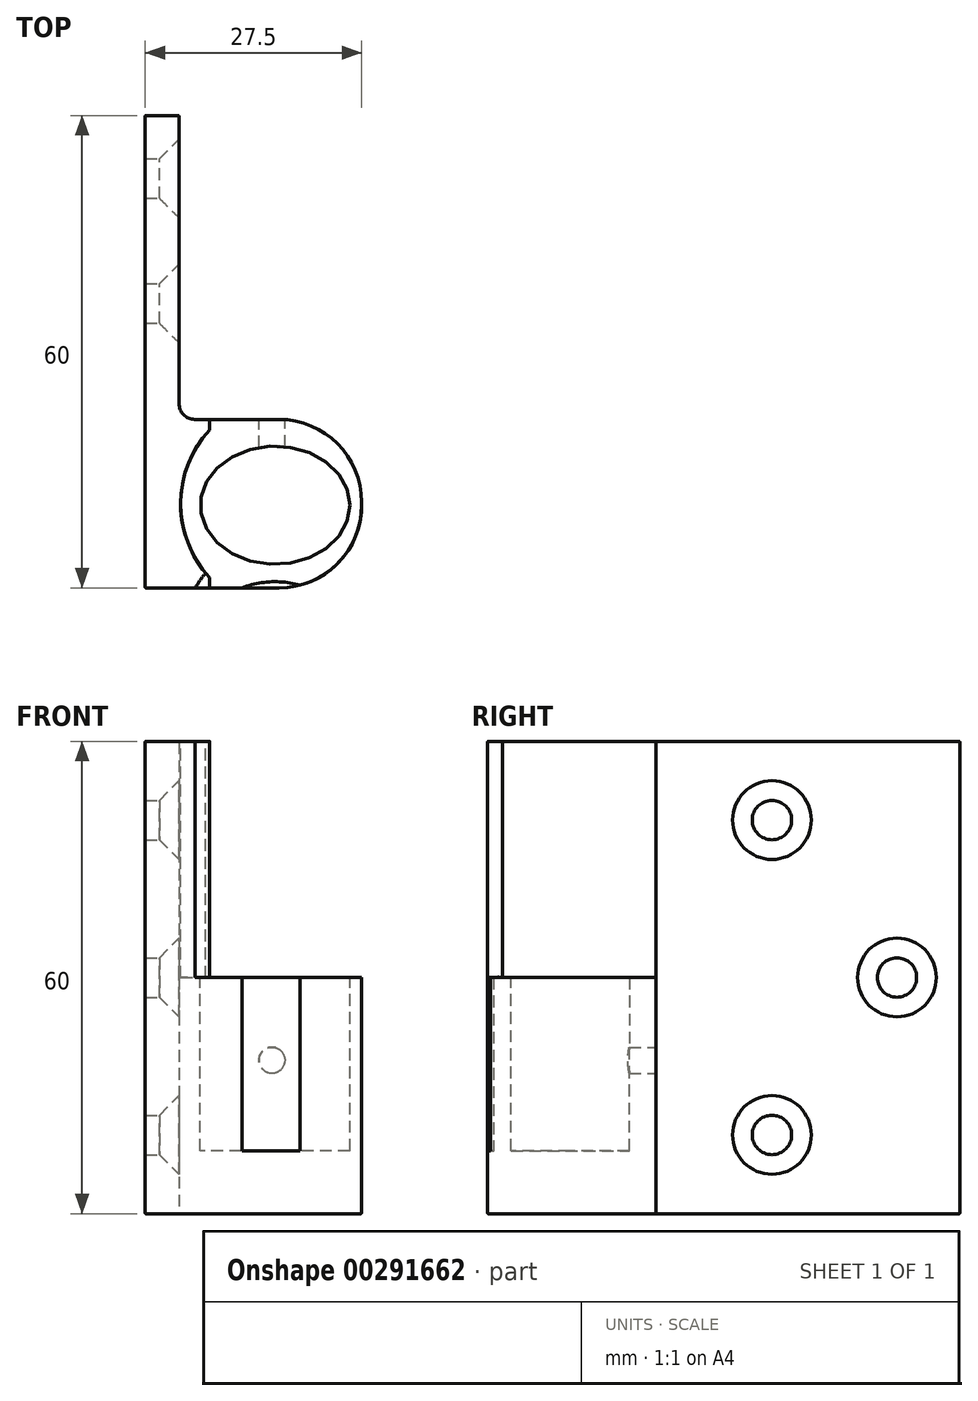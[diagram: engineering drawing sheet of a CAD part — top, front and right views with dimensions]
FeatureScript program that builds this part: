
annotation { "Feature Type Name" : "Feature", "Feature Type Description" : "" }
export const myFeature = defineFeature(function(context is Context, id is Id, definition is map)
    precondition{}
    {
        {
            var Q0;
            Q0=qCreatedBy(makeId("Top.planeOp"),FACE);
            var sketch = newSketch(context, id + "F0", { "sketchPlane" : qUnion([Q0])});
            skLineSegment(sketch, "E0", {"start": v(23.73, 6) * mm, "end": v(23.73, 6.4) * mm});
            skArc(sketch, "E1.filletArc", {"start": v(13.23, -4.5) * mm, "mid": v(20.66, -1.43) * mm, "end": v(23.73, 6) * mm});
            skArc(sketch, "E2.filletArc", {"start": v(23.73, 6.4) * mm, "mid": v(20.66, 13.82) * mm, "end": v(13.23, 16.9) * mm});
            skLineSegment(sketch, "E3.bottom", {"start": v(-3.77, -43.1) * mm, "end": v(0.53, -43.1) * mm});
            skLineSegment(sketch, "E3.left", {"start": v(-3.77, -43.1) * mm, "end": v(-3.77, 16.9) * mm});
            skLineSegment(sketch, "E3.right", {"start": v(0.53, -43.1) * mm, "end": v(0.53, -6.5) * mm});
            skLineSegment(sketch, "E4", {"start": v(-3.77, 16.9) * mm, "end": v(13.23, 16.9) * mm});
            skLineSegment(sketch, "E5", {"start": v(13.23, -4.5) * mm, "end": v(2.53, -4.5) * mm});
            skPoint(sketch, "E6.visualSharp", {"position": v(0.53, -4.5) * mm});
            skArc(sketch, "E6.filletArc", {"start": v(2.53, -4.5) * mm, "mid": v(1.12, -5.1) * mm, "end": v(0.53, -6.5) * mm});
            skSolve(sketch);
        }
        {
            var Q0;
            Q0=qSketchRegion(id+"F0",true);
            extrude(context, id + "F1", {"entities" : qUnion([Q0]), "depth" : 60 * mm});
        }
        {
            var Q0;
            Q0=makeQuery(id+"F1.opExtrude","CAP_FACE",FACE,{"disambiguationData":[OSD([sQuery(id+"F0.wireOp",EDGE,"E0"),sQuery(id+"F0.wireOp",EDGE,"E1.filletArc"),sQuery(id+"F0.wireOp",EDGE,"E2.filletArc"),sQuery(id+"F0.wireOp",EDGE,"E3.bottom"),sQuery(id+"F0.wireOp",EDGE,"E3.left"),sQuery(id+"F0.wireOp",EDGE,"E3.right"),sQuery(id+"F0.wireOp",EDGE,"E4"),sQuery(id+"F0.wireOp",EDGE,"E5"),sQuery(id+"F0.wireOp",EDGE,"E6.filletArc")])],"isStart":false});
            var sketch = newSketch(context, id + "F2", { "sketchPlane" : qUnion([Q0])});
            skLineSegment(sketch, "E7", {"start": v(4.43, 16.9) * mm, "end": v(4.43, 15.6) * mm});
            skLineSegment(sketch, "E8", {"start": v(-3.77, -4.5) * mm, "end": v(4.43, -4.5) * mm});
            skArc(sketch, "E9", {"start": v(4.43, 15.6) * mm, "mid": v(0.73, 6.2) * mm, "end": v(4.43, -3.2) * mm});
            skLineSegment(sketch, "E10", {"start": v(4.43, 16.9) * mm, "end": v(-3.77, 16.9) * mm});
            skLineSegment(sketch, "E11", {"start": v(-3.77, 16.9) * mm, "end": v(-3.77, -4.5) * mm});
            skLineSegment(sketch, "E12.trimOffspring", {"start": v(4.43, -3.2) * mm, "end": v(4.43, -4.5) * mm});
            skSolve(sketch);
        }
        {
            var Q0;
            {var subQ3=sQuery(id+"F2.wireOp",EDGE,"E7");Q0=makeQuery(id+"F2.imprint","IMPRINT",FACE,{"disambiguationData":[TD([[makeQuery(id+"F2.imprint","IMPRINT",EDGE,{"derivedFrom":subQ3}),1.0]])]});}
            extrude(context, id + "F3", {"entities" : qUnion([Q0]), "operationType" : NewBodyOperationType.REMOVE, "oppositeDirection" : true, "depth" : 30 * mm});
        }
        {
            var Q0;
            Q0=makeQuery(id+"F3.boolean.opBoolean","COPY",FACE,{"derivedFrom":makeQuery(id+"F3.opExtrude","CAP_FACE",FACE,{"disambiguationData":[OSD([sQuery(id+"F0.wireOp",EDGE,"E0"),sQuery(id+"F0.wireOp",EDGE,"E1.filletArc"),sQuery(id+"F0.wireOp",EDGE,"E2.filletArc"),sQuery(id+"F0.wireOp",EDGE,"E4"),sQuery(id+"F0.wireOp",EDGE,"E5"),sQuery(id+"F2.wireOp",EDGE,"E7"),sQuery(id+"F2.wireOp",EDGE,"E9"),sQuery(id+"F2.wireOp",EDGE,"E12.trimOffspring")])],"isStart":false})});
            var sketch = newSketch(context, id + "F4", { "sketchPlane" : qUnion([Q0])});
            skEllipse(sketch, "E13", {"center": v(12.73, 6.4) * mm, "majorRadius": 9.5 * mm, "minorRadius": 7.5 * mm, "majorAxis": v(1, 0)});
            skSolve(sketch);
        }
        {
            var Q0;
            Q0=makeQuery(id+"F4.imprint","IMPRINT",FACE,{"disambiguationData":[TD([[makeQuery(id+"F4.imprint","IMPRINT",EDGE,{"derivedFrom":sQuery(id+"F4.wireOp",EDGE,"E13")}),1.0]])]});
            extrude(context, id + "F5", {"entities" : qUnion([Q0]), "operationType" : NewBodyOperationType.REMOVE, "oppositeDirection" : true, "depth" : 22 * mm});
        }
        {
            var Q0;
            Q0=makeQuery(id+"F1.opExtrude","SWEPT_FACE",FACE,{"disambiguationData":[OSD([sQuery(id+"F0.wireOp",EDGE,"E5")])]});
            var sketch = newSketch(context, id + "F6", { "sketchPlane" : qUnion([Q0])});
            skCircle(sketch, "E14", {"center": v(12.33, 19.5) * mm, "radius": 1.5 * mm});
            skSolve(sketch);
        }
        {
            var Q0;
            Q0=sQuery(id+"F6.wireOp",VERTEX,"E14.center");
            var Q1;
            Q1=makeQuery(id+"F1.opExtrude","SWEPT_BODY",BODY,{"disambiguationData":[OSD([sQuery(id+"F0.wireOp",EDGE,"E0"),sQuery(id+"F0.wireOp",EDGE,"E1.filletArc"),sQuery(id+"F0.wireOp",EDGE,"E2.filletArc"),sQuery(id+"F0.wireOp",EDGE,"E3.bottom"),sQuery(id+"F0.wireOp",EDGE,"E3.left"),sQuery(id+"F0.wireOp",EDGE,"E3.right"),sQuery(id+"F0.wireOp",EDGE,"E4"),sQuery(id+"F0.wireOp",EDGE,"E5"),sQuery(id+"F0.wireOp",EDGE,"E6.filletArc")])]});
            hole(context, id + "F7", {"style" : HoleStyle.SIMPLE, "endStyle" : HoleEndStyle.BLIND, "standardTappedOrClearance" : lookupTablePath({ "standard" : "ISO", "fit" : "Normal", "size" : "M3", "type" : "Clearance" }), "standardBlindInLast" : lookupTablePath({ "fit" : "Standard", "standard" : "ISO", "size" : "M3", "type" : "Clearance" }), "holeDiameter" : 3.3 * mm, "holeDepth" : 8 * mm, "tappedDepth" : 10 * mm, "tapClearance" : 3, "locations" : qUnion([Q0]), "scope" : qUnion([Q1])});
        }
        {
            var Q0;
            Q0=makeQuery(id+"F1.opExtrude","SWEPT_FACE",FACE,{"disambiguationData":[OSD([sQuery(id+"F0.wireOp",EDGE,"E3.right")])]});
            var sketch = newSketch(context, id + "F8", { "sketchPlane" : qUnion([Q0])});
            skCircle(sketch, "E15", {"center": v(-19.23, 50) * mm, "radius": 2.5 * mm});
            skCircle(sketch, "E16", {"center": v(-35.1, 30) * mm, "radius": 2.5 * mm});
            skCircle(sketch, "E17", {"center": v(-19.23, 10) * mm, "radius": 2.5 * mm});
            skSolve(sketch);
        }
        {
            var Q0;
            Q0=sQuery(id+"F8.wireOp",VERTEX,"E15.center");
            var Q1;
            Q1=sQuery(id+"F8.wireOp",VERTEX,"E16.center");
            var Q2;
            Q2=sQuery(id+"F8.wireOp",VERTEX,"E17.center");
            var Q3;
            Q3=makeQuery(id+"F1.opExtrude","SWEPT_BODY",BODY,{"disambiguationData":[OSD([sQuery(id+"F0.wireOp",EDGE,"E0"),sQuery(id+"F0.wireOp",EDGE,"E1.filletArc"),sQuery(id+"F0.wireOp",EDGE,"E2.filletArc"),sQuery(id+"F0.wireOp",EDGE,"E3.bottom"),sQuery(id+"F0.wireOp",EDGE,"E3.left"),sQuery(id+"F0.wireOp",EDGE,"E3.right"),sQuery(id+"F0.wireOp",EDGE,"E4"),sQuery(id+"F0.wireOp",EDGE,"E5"),sQuery(id+"F0.wireOp",EDGE,"E6.filletArc")])]});
            hole(context, id + "F9", {"style" : HoleStyle.C_SINK, "endStyle" : HoleEndStyle.THROUGH, "holeDiameter" : 5 * mm, "cSinkDiameter" : 10 * mm, "cSinkAngle" : 90 * degree, "tappedDepth" : 10 * mm, "tapClearance" : 3, "locations" : qUnion([Q0, Q1, Q2]), "scope" : qUnion([Q3])});
        }
        {
            var Q0;
            Q0=makeQuery(id+"F1.opExtrude","CAP_EDGE",EDGE,{"disambiguationData":[OSD([sQuery(id+"F0.wireOp",EDGE,"E3.right")])],"isStart":false});
            var Q1;
            Q1=makeQuery(id+"F1.opExtrude","SWEPT_EDGE",EDGE,{"disambiguationData":[OSD([sQuery(id+"F0.wireOp",EDGE,"E3.bottom"),sQuery(id+"F0.wireOp",EDGE,"E3.right")])]});
            var Q2;
            Q2=makeQuery(id+"F1.opExtrude","CAP_EDGE",EDGE,{"disambiguationData":[OSD([sQuery(id+"F0.wireOp",EDGE,"E3.bottom")])],"isStart":false});
            var Q3;
            Q3=makeQuery(id+"F1.opExtrude","SWEPT_EDGE",EDGE,{"disambiguationData":[OSD([sQuery(id+"F0.wireOp",EDGE,"E3.bottom"),sQuery(id+"F0.wireOp",EDGE,"E3.left")])]});
            var Q4;
            Q4=makeQuery(id+"F1.opExtrude","CAP_EDGE",EDGE,{"disambiguationData":[OSD([sQuery(id+"F0.wireOp",EDGE,"E3.left")])],"isStart":false});
            var Q5;
            Q5=makeQuery(id+"F1.opExtrude","CAP_EDGE",EDGE,{"disambiguationData":[OSD([sQuery(id+"F0.wireOp",EDGE,"E3.bottom")])],"isStart":true});
            var Q6;
            Q6=makeQuery(id+"F1.opExtrude","CAP_EDGE",EDGE,{"disambiguationData":[OSD([sQuery(id+"F0.wireOp",EDGE,"E3.right")])],"isStart":true});
            var Q7;
            Q7=makeQuery(id+"F1.opExtrude","CAP_EDGE",EDGE,{"disambiguationData":[OSD([sQuery(id+"F0.wireOp",EDGE,"E3.left")])],"isStart":true});
            var Q8;
            Q8=makeQuery(id+"F1.opExtrude","SWEPT_EDGE",EDGE,{"disambiguationData":[OSD([sQuery(id+"F0.wireOp",EDGE,"E3.left"),sQuery(id+"F0.wireOp",EDGE,"E4")])]});
            var Q9;
            Q9=makeQuery(id+"F1.opExtrude","CAP_EDGE",EDGE,{"disambiguationData":[OSD([sQuery(id+"F0.wireOp",EDGE,"E4")])],"isStart":false});
            var Q10;
            Q10=makeQuery(id+"F3.boolean.opBoolean","COPY",EDGE,{"derivedFrom":makeQuery(id+"F3.opExtrude","CAP_EDGE",EDGE,{"disambiguationData":[OSD([sQuery(id+"F2.wireOp",EDGE,"E7")])],"isStart":true})});
            var Q11;
            Q11=makeQuery(id+"F1.opExtrude","CAP_EDGE",EDGE,{"disambiguationData":[OSD([sQuery(id+"F0.wireOp",EDGE,"E4")])],"isStart":true});
            var Q12;
            Q12=makeQuery(id+"F3.boolean.opBoolean","COPY",EDGE,{"derivedFrom":makeQuery(id+"F3.opExtrude","CAP_EDGE",EDGE,{"disambiguationData":[OSD([sQuery(id+"F0.wireOp",EDGE,"E4")])],"isStart":false})});
            var Q13;
            Q13=makeQuery(id+"F5.boolean.opBoolean","COPY",EDGE,{"derivedFrom":makeQuery(id+"F5.opExtrude","CAP_EDGE",EDGE,{"disambiguationData":[OSD([sQuery(id+"F4.wireOp",EDGE,"E13")])],"isStart":true})});
            var Q14;
            Q14=makeQuery(id+"F3.boolean.opBoolean","COPY",EDGE,{"derivedFrom":makeQuery(id+"F3.opExtrude","SWEPT_EDGE",EDGE,{"disambiguationData":[OSD([sQuery(id+"F0.wireOp",EDGE,"E4"),sQuery(id+"F2.wireOp",EDGE,"E7"),sQuery(id+"F2.wireOp",EDGE,"E10")])]})});
            var Q15;
            Q15=makeQuery(id+"F3.boolean.opBoolean","COPY",EDGE,{"derivedFrom":makeQuery(id+"F3.opExtrude","SWEPT_EDGE",EDGE,{"disambiguationData":[OSD([sQuery(id+"F0.wireOp",EDGE,"E5"),sQuery(id+"F2.wireOp",EDGE,"E8"),sQuery(id+"F2.wireOp",EDGE,"E12.trimOffspring")])]})});
            var Q16;
            Q16=makeQuery(id+"F3.boolean.opBoolean","COPY",EDGE,{"derivedFrom":makeQuery(id+"F3.opExtrude","CAP_EDGE",EDGE,{"disambiguationData":[OSD([sQuery(id+"F2.wireOp",EDGE,"E12.trimOffspring")])],"isStart":false})});
            var Q17;
            Q17=makeQuery(id+"F3.boolean.opBoolean","COPY",EDGE,{"derivedFrom":makeQuery(id+"F3.opExtrude","CAP_EDGE",EDGE,{"disambiguationData":[OSD([sQuery(id+"F2.wireOp",EDGE,"E7")])],"isStart":false})});
            var Q18;
            Q18=makeQuery(id+"F3.boolean.opBoolean","COPY",EDGE,{"derivedFrom":makeQuery(id+"F3.opExtrude","CAP_EDGE",EDGE,{"disambiguationData":[OSD([sQuery(id+"F2.wireOp",EDGE,"E12.trimOffspring")])],"isStart":true})});
            var Q19;
            Q19=makeQuery(id+"F3.boolean.opBoolean","COPY",EDGE,{"derivedFrom":makeQuery(id+"F3.opExtrude","CAP_EDGE",EDGE,{"disambiguationData":[OSD([sQuery(id+"F2.wireOp",EDGE,"E9")])],"isStart":true})});
            var Q20;
            Q20=makeQuery(id+"F3.boolean.opBoolean","COPY",EDGE,{"derivedFrom":makeQuery(id+"F3.opExtrude","SWEPT_EDGE",EDGE,{"disambiguationData":[OSD([sQuery(id+"F2.wireOp",EDGE,"E7"),sQuery(id+"F2.wireOp",EDGE,"E9")])]})});
            var Q21;
            Q21=makeQuery(id+"F3.boolean.opBoolean","COPY",EDGE,{"derivedFrom":makeQuery(id+"F3.opExtrude","SWEPT_EDGE",EDGE,{"disambiguationData":[OSD([sQuery(id+"F2.wireOp",EDGE,"E9"),sQuery(id+"F2.wireOp",EDGE,"E12.trimOffspring")])]})});
            fillet(context, id + "F10", {"entities" : qUnion([Q0, Q1, Q2, Q3, Q4, Q5, Q6, Q7, Q8, Q9, Q10, Q11, Q12, Q13, Q14, Q15, Q16, Q17, Q18, Q19, Q20, Q21]), "radius" : 0.1 * mm, "tangentPropagation" : true, "allowEdgeOverflow" : false});
        }
        {
            var Q0;
            Q0=makeQuery(id+"F1.opExtrude","SWEPT_BODY",BODY,{"disambiguationData":[OSD([sQuery(id+"F0.wireOp",EDGE,"E0"),sQuery(id+"F0.wireOp",EDGE,"E1.filletArc"),sQuery(id+"F0.wireOp",EDGE,"E2.filletArc"),sQuery(id+"F0.wireOp",EDGE,"E3.bottom"),sQuery(id+"F0.wireOp",EDGE,"E3.left"),sQuery(id+"F0.wireOp",EDGE,"E3.right"),sQuery(id+"F0.wireOp",EDGE,"E4"),sQuery(id+"F0.wireOp",EDGE,"E5"),sQuery(id+"F0.wireOp",EDGE,"E6.filletArc")])]});
            var Q1;
            {var subQ0=sQuery(id+"F0.wireOp",EDGE,"E3.right");Q1=makeQuery(id+"F10.opFillet","BLEND_EDGE",EDGE,{"blendedFrom":[makeQuery(id+"F1.opExtrude","CAP_EDGE",EDGE,{"disambiguationData":[OSD([subQ0])],"isStart":false}),makeQuery(id+"F1.opExtrude","SWEPT_FACE",FACE,{"disambiguationData":[OSD([subQ0])]})],"blendedInto":[makeQuery(id+"F1.opExtrude","SWEPT_FACE",FACE,{"disambiguationData":[OSD([subQ0])]})]});}
            transform(context, id + "F11", {"entities" : qUnion([Q0]), "transformType" : TransformType.TRANSLATION_DISTANCE, "transformDirection" : qUnion([Q1]), "distance" : 30 * mm, "makeCopy" : false});
        }
        {
            var Q0;
            Q0=makeQuery(id+"F1.opExtrude","SWEPT_BODY",BODY,{"disambiguationData":[OSD([sQuery(id+"F0.wireOp",EDGE,"E0"),sQuery(id+"F0.wireOp",EDGE,"E1.filletArc"),sQuery(id+"F0.wireOp",EDGE,"E2.filletArc"),sQuery(id+"F0.wireOp",EDGE,"E3.bottom"),sQuery(id+"F0.wireOp",EDGE,"E3.left"),sQuery(id+"F0.wireOp",EDGE,"E3.right"),sQuery(id+"F0.wireOp",EDGE,"E4"),sQuery(id+"F0.wireOp",EDGE,"E5"),sQuery(id+"F0.wireOp",EDGE,"E6.filletArc")])]});
            var Q1;
            Q1=qCreatedBy(makeId("Front.planeOp"),FACE);
            mirror(context, id + "F12", {"entities" : qUnion([Q0]), "mirrorPlane" : qUnion([Q1])});
        }
        {
            var Q0;
            Q0=makeQuery(id+"F1.opExtrude","SWEPT_BODY",BODY,{"disambiguationData":[OSD([sQuery(id+"F0.wireOp",EDGE,"E0"),sQuery(id+"F0.wireOp",EDGE,"E1.filletArc"),sQuery(id+"F0.wireOp",EDGE,"E2.filletArc"),sQuery(id+"F0.wireOp",EDGE,"E3.bottom"),sQuery(id+"F0.wireOp",EDGE,"E3.left"),sQuery(id+"F0.wireOp",EDGE,"E3.right"),sQuery(id+"F0.wireOp",EDGE,"E4"),sQuery(id+"F0.wireOp",EDGE,"E5"),sQuery(id+"F0.wireOp",EDGE,"E6.filletArc")])]});
            deleteBodies(context, id + "F13", {"entities" : qUnion([Q0])});
        }
    });
